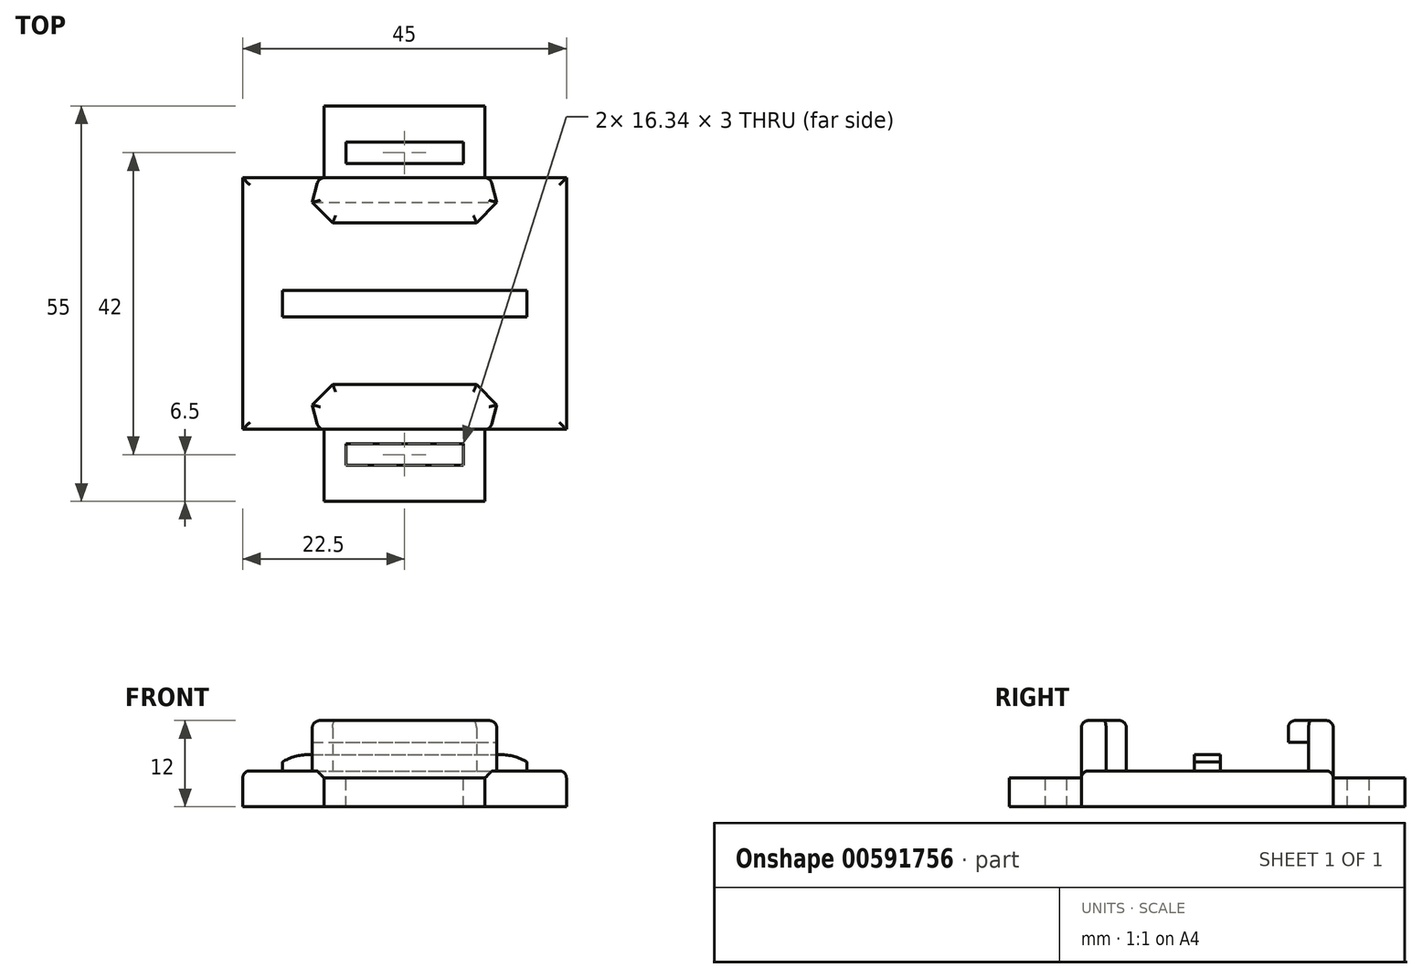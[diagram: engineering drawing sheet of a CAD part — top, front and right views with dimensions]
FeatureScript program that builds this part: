
annotation { "Feature Type Name" : "Feature", "Feature Type Description" : "" }
export const myFeature = defineFeature(function(context is Context, id is Id, definition is map)
    precondition{}
    {
        {
            var Q0;
            Q0=qCreatedBy(makeId("Top.planeOp"),FACE);
            var sketch = newSketch(context, id + "F0", { "sketchPlane" : qUnion([Q0])});
            skLineSegment(sketch, "E0.rect.bottom", {"start": v(-22.5, 17.5) * mm, "end": v(22.5, 17.5) * mm});
            skLineSegment(sketch, "E0.rect.top", {"start": v(-22.5, -17.5) * mm, "end": v(22.5, -17.5) * mm});
            skLineSegment(sketch, "E0.rect.left", {"start": v(-22.5, 17.5) * mm, "end": v(-22.5, -17.5) * mm});
            skLineSegment(sketch, "E0.rect.right", {"start": v(22.5, 17.5) * mm, "end": v(22.5, -17.5) * mm});
            skPoint(sketch, "E0.rect.middle", {"position": v(0, 0) * mm});
            skSolve(sketch);
        }
        {
            var Q0;
            Q0=makeQuery(id+"F0.imprint","IMPRINT",FACE,{"disambiguationData":[TD([[makeQuery(id+"F0.imprint","IMPRINT",EDGE,{"derivedFrom":sQuery(id+"F0.wireOp",EDGE,"E0.rect.bottom")}),-1.0]])]});
            extrude(context, id + "F1", {"entities" : qUnion([Q0]), "depth" : 5 * mm});
        }
        {
            var Q0;
            Q0=makeQuery(id+"F1.opExtrude","CAP_FACE",FACE,{"disambiguationData":[OSD([sQuery(id+"F0.wireOp",EDGE,"E0.rect.bottom"),sQuery(id+"F0.wireOp",EDGE,"E0.rect.top"),sQuery(id+"F0.wireOp",EDGE,"E0.rect.left"),sQuery(id+"F0.wireOp",EDGE,"E0.rect.right")])],"isStart":false});
            var sketch = newSketch(context, id + "F2", { "sketchPlane" : qUnion([Q0])});
            skLineSegment(sketch, "E1.rect.bottom", {"start": v(-17, 1.82) * mm, "end": v(17, 1.82) * mm});
            skLineSegment(sketch, "E1.rect.top", {"start": v(-17, -1.83) * mm, "end": v(17, -1.83) * mm});
            skLineSegment(sketch, "E1.rect.left", {"start": v(-17, 1.82) * mm, "end": v(-17, -1.83) * mm});
            skLineSegment(sketch, "E1.rect.right", {"start": v(17, 1.82) * mm, "end": v(17, -1.83) * mm});
            skPoint(sketch, "E1.rect.middle", {"position": v(0, 0) * mm});
            skSolve(sketch);
        }
        {
            var Q0;
            Q0=makeQuery(id+"F2.imprint","IMPRINT",FACE,{"disambiguationData":[TD([[makeQuery(id+"F2.imprint","IMPRINT",EDGE,{"derivedFrom":sQuery(id+"F2.wireOp",EDGE,"E1.rect.bottom")}),-1.0]])]});
            extrude(context, id + "F3", {"entities" : qUnion([Q0]), "operationType" : NewBodyOperationType.ADD, "depth" : 2.25 * mm});
        }
        {
            var Q0;
            Q0=makeQuery(id+"F3.opExtrude","SWEPT_FACE",FACE,{"disambiguationData":[OSD([sQuery(id+"F2.wireOp",EDGE,"E1.rect.top")])]});
            var sketch = newSketch(context, id + "F4", { "sketchPlane" : qUnion([Q0])});
            skLineSegment(sketch, "E2", {"start": v(-17, 7.25) * mm, "end": v(17, 7.25) * mm, "construction": true});
            skLineSegment(sketch, "E3.0", {"start": v(-17, 6.25) * mm, "end": v(17, 6.25) * mm});
            skArc(sketch, "E4", {"start": v(-13.26, 7.25) * mm, "mid": v(-15.2, 7) * mm, "end": v(-17, 6.25) * mm});
            skLineSegment(sketch, "E5", {"start": v(0, 0) * mm, "end": v(0, 15.47) * mm, "construction": true});
            skArc(sketch, "E6.0.MirrorCS", {"start": v(13.26, 7.25) * mm, "mid": v(15.2, 7) * mm, "end": v(17, 6.25) * mm});
            skLineSegment(sketch, "E7", {"start": v(-17, 6.25) * mm, "end": v(-18.16, 6.25) * mm});
            skLineSegment(sketch, "E8", {"start": v(-18.16, 6.25) * mm, "end": v(-18.16, 8.7) * mm});
            skLineSegment(sketch, "E9", {"start": v(-18.16, 8.7) * mm, "end": v(-13.25, 8.7) * mm});
            skLineSegment(sketch, "E10", {"start": v(-13.25, 8.7) * mm, "end": v(-13.26, 7.25) * mm});
            skLineSegment(sketch, "E11", {"start": v(13.26, 7.25) * mm, "end": v(13.26, 8.4) * mm});
            skLineSegment(sketch, "E12", {"start": v(13.26, 8.4) * mm, "end": v(18.11, 8.4) * mm});
            skLineSegment(sketch, "E13", {"start": v(18.11, 8.4) * mm, "end": v(18.11, 6.28) * mm});
            skLineSegment(sketch, "E14", {"start": v(18.11, 6.28) * mm, "end": v(17, 6.25) * mm});
            skSolve(sketch);
        }
        {
            var Q0;
            {var subQ0=sQuery(id+"F2.wireOp",EDGE,"E1.rect.top");var subQ1=makeQuery(id+"F3.opExtrude","CAP_EDGE",EDGE,{"disambiguationData":[OSD([subQ0])],"isStart":false});var subQ2=sQuery(id+"F4.wireOp",EDGE,"E4");var subQ3=makeQuery(id+"F4.imprint","INTERSECT",VERTEX,{"derivedFrom":[subQ1,subQ2]});var subQ6=makeQuery(id+"F4.imprint","IMPRINT",EDGE,{"disambiguationData":[TD([[subQ3,1.0]])],"derivedFrom":subQ1});var subQ8=sQuery(id+"F4.wireOp",EDGE,"E7");var subQ13=sQuery(id+"F4.wireOp",EDGE,"E6.0.MirrorCS");var subQ18=makeQuery(id+"F4.imprint","INTERSECT",VERTEX,{"derivedFrom":[subQ1,subQ13]});var subQ19=makeQuery(id+"F4.imprint","IMPRINT",EDGE,{"disambiguationData":[TD([[subQ18,-1.0]])],"derivedFrom":subQ1});var subQ20=sQuery(id+"F4.wireOp",EDGE,"E11");Q0=qUnion([makeQuery(id+"F4.imprint","IMPRINT",FACE,{"disambiguationData":[TD([[makeQuery(id+"F4.imprint","IMPRINT",EDGE,{"derivedFrom":subQ8}),-1.0]])]}),makeQuery(id+"F4.imprint","IMPRINT",FACE,{"disambiguationData":[TD([[subQ6,-1.0]])]}),makeQuery(id+"F4.imprint","IMPRINT",FACE,{"disambiguationData":[TD([[makeQuery(id+"F4.imprint","IMPRINT",EDGE,{"derivedFrom":subQ20}),-1.0]])]}),makeQuery(id+"F4.imprint","IMPRINT",FACE,{"disambiguationData":[TD([[subQ19,-1.0]])]})]);}
            extrude(context, id + "F5", {"entities" : qUnion([Q0]), "operationType" : NewBodyOperationType.REMOVE, "endBound" : BoundingType.THROUGH_ALL, "oppositeDirection" : true, "depth" : 25 * mm});
        }
        {
            var Q0;
            Q0=makeQuery(id+"F1.opExtrude","CAP_FACE",FACE,{"disambiguationData":[OSD([sQuery(id+"F0.wireOp",EDGE,"E0.rect.bottom"),sQuery(id+"F0.wireOp",EDGE,"E0.rect.top"),sQuery(id+"F0.wireOp",EDGE,"E0.rect.left"),sQuery(id+"F0.wireOp",EDGE,"E0.rect.right")])],"isStart":false});
            var sketch = newSketch(context, id + "F6", { "sketchPlane" : qUnion([Q0])});
            skLineSegment(sketch, "E15.rect.bottom", {"start": v(-11.94, 17.5) * mm, "end": v(11.94, 17.5) * mm, "construction": true});
            skPoint(sketch, "E15.rect.middle", {"position": v(0, 0) * mm});
            skLineSegment(sketch, "E16.0", {"start": v(-10, 11.25) * mm, "end": v(10, 11.25) * mm});
            skLineSegment(sketch, "E17", {"start": v(-10, 11.25) * mm, "end": v(-12.82, 14.08) * mm, "construction": true});
            skLineSegment(sketch, "E18.0.MirrorCS", {"start": v(10, 11.25) * mm, "end": v(12.82, 14.08) * mm, "construction": true});
            skLineSegment(sketch, "E19", {"start": v(10, 11.25) * mm, "end": v(12.82, 14.08) * mm});
            skLineSegment(sketch, "E20", {"start": v(11.94, 17.5) * mm, "end": v(-11.94, 17.5) * mm});
            skLineSegment(sketch, "E21", {"start": v(-12.82, 14.08) * mm, "end": v(-10, 11.25) * mm});
            skLineSegment(sketch, "E22.0.MirrorCS", {"start": v(-10, -11.25) * mm, "end": v(-12.82, -14.08) * mm, "construction": true});
            skLineSegment(sketch, "E22.1.MirrorCS", {"start": v(-11.94, -17.5) * mm, "end": v(11.94, -17.5) * mm, "construction": true});
            skLineSegment(sketch, "E22.2.MirrorCS", {"start": v(-11.94, -17.5) * mm, "end": v(11.94, -17.5) * mm, "construction": true});
            skLineSegment(sketch, "E22.4.MirrorCS", {"start": v(-10, -11.25) * mm, "end": v(-12.82, -14.08) * mm, "construction": true});
            skLineSegment(sketch, "E22.5.MirrorCS", {"start": v(10, -11.25) * mm, "end": v(12.82, -14.08) * mm, "construction": true});
            skLineSegment(sketch, "E22.7.MirrorCS", {"start": v(11.94, -17.5) * mm, "end": v(-11.94, -17.5) * mm});
            skLineSegment(sketch, "E22.9.MirrorCS", {"start": v(10, -11.25) * mm, "end": v(12.82, -14.08) * mm});
            skLineSegment(sketch, "E22.10.MirrorCS", {"start": v(-12.82, -14.08) * mm, "end": v(-10, -11.25) * mm});
            skLineSegment(sketch, "E22.12.MirrorCS", {"start": v(-10, -11.25) * mm, "end": v(10, -11.25) * mm});
            skLineSegment(sketch, "E23", {"start": v(12.82, 14.08) * mm, "end": v(11.94, 17.5) * mm});
            skLineSegment(sketch, "E24.0.MirrorCS", {"start": v(12.82, -14.08) * mm, "end": v(11.94, -17.5) * mm});
            skLineSegment(sketch, "E25.0.MirrorCS", {"start": v(-12.82, 14.08) * mm, "end": v(-11.94, 17.5) * mm});
            skLineSegment(sketch, "E26.0.MirrorCS", {"start": v(-12.82, -14.08) * mm, "end": v(-11.94, -17.5) * mm});
            skSolve(sketch);
        }
        {
            var Q0;
            {Q0=qUnion([makeQuery(id+"F6.imprint","IMPRINT",FACE,{"disambiguationData":[TD([[makeQuery(id+"F6.imprint","IMPRINT",EDGE,{"derivedFrom":sQuery(id+"F6.wireOp",EDGE,"E16.0")}),1.0]])]}),makeQuery(id+"F6.imprint","IMPRINT",FACE,{"disambiguationData":[TD([[makeQuery(id+"F6.imprint","IMPRINT",EDGE,{"derivedFrom":sQuery(id+"F6.wireOp",EDGE,"E22.7.MirrorCS")}),1.0]])]})]);}
            extrude(context, id + "F7", {"entities" : qUnion([Q0]), "operationType" : NewBodyOperationType.ADD, "depth" : 7 * mm});
        }
        {
            var Q0;
            Q0=qCreatedBy(makeId("Right.planeOp"),FACE);
            var sketch = newSketch(context, id + "F8", { "sketchPlane" : qUnion([Q0])});
            skLineSegment(sketch, "E27.0", {"start": v(14.1, 9) * mm, "end": v(14.1, 5) * mm});
            skLineSegment(sketch, "E28.bottom", {"start": v(14.1, 5) * mm, "end": v(10.15, 5) * mm});
            skLineSegment(sketch, "E28.top", {"start": v(14.1, 9) * mm, "end": v(10.15, 9) * mm});
            skLineSegment(sketch, "E28.left", {"start": v(14.1, 5) * mm, "end": v(14.1, 9) * mm});
            skLineSegment(sketch, "E28.right", {"start": v(10.15, 5) * mm, "end": v(10.15, 9) * mm});
            skLineSegment(sketch, "E29.0.MirrorCS", {"start": v(-14.1, 5) * mm, "end": v(-14.1, 9) * mm});
            skLineSegment(sketch, "E29.1.MirrorCS", {"start": v(-14.1, 9) * mm, "end": v(-14.1, 5) * mm});
            skLineSegment(sketch, "E29.2.MirrorCS", {"start": v(-14.1, 9) * mm, "end": v(-10.15, 9) * mm});
            skLineSegment(sketch, "E29.3.MirrorCS", {"start": v(-10.15, 5) * mm, "end": v(-10.15, 9) * mm});
            skLineSegment(sketch, "E29.4.MirrorCS", {"start": v(-14.1, 5) * mm, "end": v(-10.15, 5) * mm});
            skSolve(sketch);
        }
        {
            var Q0;
            {Q0=qUnion([makeQuery(id+"F8.imprint","IMPRINT",FACE,{"disambiguationData":[TD([[makeQuery(id+"F8.imprint","IMPRINT",EDGE,{"derivedFrom":sQuery(id+"F8.wireOp",EDGE,"E28.bottom")}),-1.0]])]}),makeQuery(id+"F8.imprint","IMPRINT",FACE,{"disambiguationData":[TD([[makeQuery(id+"F8.imprint","IMPRINT",EDGE,{"derivedFrom":sQuery(id+"F8.wireOp",EDGE,"E29.1.MirrorCS")}),1.0]])]})]);}
            extrude(context, id + "F9", {"entities" : qUnion([Q0]), "operationType" : NewBodyOperationType.REMOVE, "endBound" : BoundingType.SYMMETRIC, "oppositeDirection" : true, "depth" : 31.01 * mm});
        }
        {
            var Q0;
            Q0=makeQuery(id+"F7.opExtrude","CAP_FACE",FACE,{"disambiguationData":[OSD([sQuery(id+"F6.wireOp",EDGE,"E16.0"),sQuery(id+"F6.wireOp",EDGE,"E19"),sQuery(id+"F6.wireOp",EDGE,"E20"),sQuery(id+"F6.wireOp",EDGE,"E21"),sQuery(id+"F6.wireOp",EDGE,"E23"),sQuery(id+"F6.wireOp",EDGE,"E25.0.MirrorCS")])],"isStart":false});
            var Q1;
            Q1=makeQuery(id+"F7.opExtrude","CAP_FACE",FACE,{"disambiguationData":[OSD([sQuery(id+"F6.wireOp",EDGE,"E22.7.MirrorCS"),sQuery(id+"F6.wireOp",EDGE,"E22.9.MirrorCS"),sQuery(id+"F6.wireOp",EDGE,"E22.10.MirrorCS"),sQuery(id+"F6.wireOp",EDGE,"E22.12.MirrorCS"),sQuery(id+"F6.wireOp",EDGE,"E24.0.MirrorCS"),sQuery(id+"F6.wireOp",EDGE,"E26.0.MirrorCS")])],"isStart":false});
            var Q2;
            Q2=makeQuery(id+"F7.opExtrude","SWEPT_EDGE",EDGE,{"disambiguationData":[OSD([sQuery(id+"F0.wireOp",EDGE,"E0.rect.bottom"),sQuery(id+"F6.wireOp",EDGE,"E20"),sQuery(id+"F6.wireOp",EDGE,"E23")])]});
            var Q3;
            Q3=makeQuery(id+"F7.opExtrude","SWEPT_EDGE",EDGE,{"disambiguationData":[OSD([sQuery(id+"F0.wireOp",EDGE,"E0.rect.bottom"),sQuery(id+"F6.wireOp",EDGE,"E20"),sQuery(id+"F6.wireOp",EDGE,"E25.0.MirrorCS")])]});
            var Q4;
            Q4=makeQuery(id+"F7.opExtrude","SWEPT_EDGE",EDGE,{"disambiguationData":[OSD([sQuery(id+"F0.wireOp",EDGE,"E0.rect.top"),sQuery(id+"F6.wireOp",EDGE,"E22.7.MirrorCS"),sQuery(id+"F6.wireOp",EDGE,"E24.0.MirrorCS")])]});
            var Q5;
            Q5=makeQuery(id+"F7.opExtrude","SWEPT_EDGE",EDGE,{"disambiguationData":[OSD([sQuery(id+"F0.wireOp",EDGE,"E0.rect.top"),sQuery(id+"F6.wireOp",EDGE,"E22.7.MirrorCS"),sQuery(id+"F6.wireOp",EDGE,"E26.0.MirrorCS")])]});
            fillet(context, id + "F10", {"entities" : qUnion([Q0, Q1, Q2, Q3, Q4, Q5]), "radius" : 1 * mm, "tangentPropagation" : true, "allowEdgeOverflow" : false});
        }
        {
            var Q0;
            {var subQ0=sQuery(id+"F0.wireOp",EDGE,"E0.rect.top");var subQ1=sQuery(id+"F0.wireOp",EDGE,"E0.rect.right");Q0=makeQuery(id+"F7.boolean.opBoolean","SPLIT",EDGE,{"disambiguationData":[TD([makeQuery(id+"F1.opExtrude","SWEPT_FACE",FACE,{"disambiguationData":[OSD([subQ1])]})])],"derivedFrom":makeQuery(id+"F1.opExtrude","CAP_EDGE",EDGE,{"disambiguationData":[OSD([subQ0])],"isStart":false})});}
            var Q1;
            Q1=makeQuery(id+"F1.opExtrude","CAP_EDGE",EDGE,{"disambiguationData":[OSD([sQuery(id+"F0.wireOp",EDGE,"E0.rect.right")])],"isStart":false});
            var Q2;
            {var subQ0=sQuery(id+"F0.wireOp",EDGE,"E0.rect.bottom");var subQ1=sQuery(id+"F0.wireOp",EDGE,"E0.rect.right");Q2=makeQuery(id+"F7.boolean.opBoolean","SPLIT",EDGE,{"disambiguationData":[TD([makeQuery(id+"F1.opExtrude","SWEPT_FACE",FACE,{"disambiguationData":[OSD([subQ1])]})])],"derivedFrom":makeQuery(id+"F1.opExtrude","CAP_EDGE",EDGE,{"disambiguationData":[OSD([subQ0])],"isStart":false})});}
            var Q3;
            {var subQ0=sQuery(id+"F0.wireOp",EDGE,"E0.rect.bottom");var subQ1=sQuery(id+"F0.wireOp",EDGE,"E0.rect.left");Q3=makeQuery(id+"F7.boolean.opBoolean","SPLIT",EDGE,{"disambiguationData":[TD([makeQuery(id+"F1.opExtrude","SWEPT_FACE",FACE,{"disambiguationData":[OSD([subQ1])]})])],"derivedFrom":makeQuery(id+"F1.opExtrude","CAP_EDGE",EDGE,{"disambiguationData":[OSD([subQ0])],"isStart":false})});}
            var Q4;
            Q4=makeQuery(id+"F1.opExtrude","CAP_EDGE",EDGE,{"disambiguationData":[OSD([sQuery(id+"F0.wireOp",EDGE,"E0.rect.left")])],"isStart":false});
            var Q5;
            {var subQ0=sQuery(id+"F0.wireOp",EDGE,"E0.rect.top");var subQ1=sQuery(id+"F0.wireOp",EDGE,"E0.rect.left");Q5=makeQuery(id+"F7.boolean.opBoolean","SPLIT",EDGE,{"disambiguationData":[TD([makeQuery(id+"F1.opExtrude","SWEPT_FACE",FACE,{"disambiguationData":[OSD([subQ1])]})])],"derivedFrom":makeQuery(id+"F1.opExtrude","CAP_EDGE",EDGE,{"disambiguationData":[OSD([subQ0])],"isStart":false})});}
            fillet(context, id + "F11", {"entities" : qUnion([Q0, Q1, Q2, Q3, Q4, Q5]), "radius" : 1 * mm, "allowEdgeOverflow" : false});
        }
        {
            var Q0;
            Q0=makeQuery(id+"F7.boolean.opBoolean","MERGE",FACE,{"derivedFrom":[makeQuery(id+"F1.opExtrude","SWEPT_FACE",FACE,{"disambiguationData":[OSD([sQuery(id+"F0.wireOp",EDGE,"E0.rect.bottom")])]}),makeQuery(id+"F7.opExtrude","SWEPT_FACE",FACE,{"disambiguationData":[OSD([sQuery(id+"F6.wireOp",EDGE,"E20")])]})]});
            var sketch = newSketch(context, id + "F12", { "sketchPlane" : qUnion([Q0])});
            skLineSegment(sketch, "E30.0", {"start": v(22.5, 0) * mm, "end": v(-22.5, 0) * mm});
            skLineSegment(sketch, "E31.0", {"start": v(11.17, 11) * mm, "end": v(-11.17, 11) * mm});
            skLineSegment(sketch, "E32", {"start": v(-11.17, 11) * mm, "end": v(-11.17, 0) * mm, "construction": true});
            skLineSegment(sketch, "E33", {"start": v(11.17, 11) * mm, "end": v(11.17, 0) * mm, "construction": true});
            skLineSegment(sketch, "E34", {"start": v(-11.17, 4) * mm, "end": v(11.17, 4) * mm});
            skLineSegment(sketch, "E35", {"start": v(11.17, 4) * mm, "end": v(11.17, 0) * mm});
            skLineSegment(sketch, "E36", {"start": v(-11.17, 0) * mm, "end": v(-11.17, 4) * mm});
            skSolve(sketch);
        }
        {
            var Q0;
            Q0 = qSketchRegion(id + "F12", true);
            extrude(context, id + "F13", {"entities" : qUnion([Q0]), "operationType" : NewBodyOperationType.ADD, "depth" : 10 * mm, "offsetDistance" : 25 * mm});
        }
        {
            var Q0;
            Q0=makeQuery(id+"F7.boolean.opBoolean","MERGE",FACE,{"derivedFrom":[makeQuery(id+"F1.opExtrude","SWEPT_FACE",FACE,{"disambiguationData":[OSD([sQuery(id+"F0.wireOp",EDGE,"E0.rect.top")])]}),makeQuery(id+"F7.opExtrude","SWEPT_FACE",FACE,{"disambiguationData":[OSD([sQuery(id+"F6.wireOp",EDGE,"E22.7.MirrorCS")])]})]});
            var sketch = newSketch(context, id + "F14", { "sketchPlane" : qUnion([Q0])});
            skLineSegment(sketch, "E37.0", {"start": v(11.17, 11) * mm, "end": v(-11.17, 11) * mm});
            skLineSegment(sketch, "E38.0", {"start": v(-22.5, 0) * mm, "end": v(22.5, 0) * mm});
            skLineSegment(sketch, "E39", {"start": v(-11.17, 11) * mm, "end": v(-11.17, 0) * mm, "construction": true});
            skLineSegment(sketch, "E40", {"start": v(11.17, 11) * mm, "end": v(11.17, 0) * mm, "construction": true});
            skPoint(sketch, "E40.endSnap0", {"position": v(11.17, 7.5) * mm});
            skLineSegment(sketch, "E41", {"start": v(-11.17, 4) * mm, "end": v(11.17, 4) * mm});
            skLineSegment(sketch, "E42", {"start": v(11.17, 4) * mm, "end": v(11.17, 0) * mm});
            skLineSegment(sketch, "E43", {"start": v(-11.17, 0) * mm, "end": v(-11.17, 4) * mm});
            skSolve(sketch);
        }
        {
            var Q0;
            Q0=makeQuery(id+"F14.imprint","IMPRINT",FACE,{"disambiguationData":[TD([[makeQuery(id+"F14.imprint","IMPRINT",EDGE,{"derivedFrom":sQuery(id+"F14.wireOp",EDGE,"E41")}),-1.0]])]});
            extrude(context, id + "F15", {"entities" : qUnion([Q0]), "operationType" : NewBodyOperationType.ADD, "depth" : 10 * mm, "offsetDistance" : 25 * mm});
        }
        {
            var Q0;
            Q0=makeQuery(id+"F15.opExtrude","SWEPT_FACE",FACE,{"disambiguationData":[OSD([sQuery(id+"F14.wireOp",EDGE,"E41")])]});
            var sketch = newSketch(context, id + "F16", { "sketchPlane" : qUnion([Q0])});
            skLineSegment(sketch, "E44.0", {"start": v(-11.17, -27.5) * mm, "end": v(11.17, -27.5) * mm});
            skLineSegment(sketch, "E45.0", {"start": v(-11.17, -17.5) * mm, "end": v(11.17, -17.5) * mm});
            skLineSegment(sketch, "E46.0", {"start": v(-11.17, -27.5) * mm, "end": v(-11.17, -17.5) * mm});
            skLineSegment(sketch, "E47.0", {"start": v(11.17, -27.5) * mm, "end": v(11.17, -17.5) * mm});
            skLineSegment(sketch, "E48.bottom", {"start": v(-11.17, -22.5) * mm, "end": v(11.17, -22.5) * mm});
            skLineSegment(sketch, "E48.top", {"start": v(-11.17, -19.5) * mm, "end": v(11.17, -19.5) * mm});
            skLineSegment(sketch, "E48.left", {"start": v(-11.17, -22.5) * mm, "end": v(-11.17, -19.5) * mm});
            skLineSegment(sketch, "E48.right", {"start": v(11.17, -22.5) * mm, "end": v(11.17, -19.5) * mm});
            skLineSegment(sketch, "E49", {"start": v(-8.17, -19.5) * mm, "end": v(-8.17, -22.5) * mm});
            skLineSegment(sketch, "E50", {"start": v(8.17, -19.5) * mm, "end": v(8.17, -22.5) * mm});
            skLineSegment(sketch, "E51", {"start": v(-11.17, -21) * mm, "end": v(-8.17, -21) * mm, "construction": true});
            skLineSegment(sketch, "E52", {"start": v(8.17, -21) * mm, "end": v(11.17, -21) * mm, "construction": true});
            skSolve(sketch);
        }
        {
            var Q0;
            {var subQ0=sQuery(id+"F16.wireOp",EDGE,"E49");Q0=makeQuery(id+"F16.imprint","IMPRINT",FACE,{"disambiguationData":[TD([[makeQuery(id+"F16.imprint","IMPRINT",EDGE,{"derivedFrom":subQ0}),1.0]])]});}
            extrude(context, id + "F17", {"entities" : qUnion([Q0]), "operationType" : NewBodyOperationType.REMOVE, "oppositeDirection" : true, "depth" : 25 * mm, "offsetDistance" : 25 * mm});
        }
        {
            var Q0;
            Q0=makeQuery(id+"F13.opExtrude","SWEPT_FACE",FACE,{"disambiguationData":[OSD([sQuery(id+"F12.wireOp",EDGE,"E34")])]});
            var sketch = newSketch(context, id + "F18", { "sketchPlane" : qUnion([Q0])});
            skLineSegment(sketch, "E53", {"start": v(-11.17, 22.5) * mm, "end": v(11.17, 22.5) * mm});
            skLineSegment(sketch, "E54", {"start": v(-11.17, 19.5) * mm, "end": v(11.17, 19.5) * mm});
            skLineSegment(sketch, "E55", {"start": v(-8.55, 22.5) * mm, "end": v(-8.55, 19.5) * mm, "construction": true});
            skLineSegment(sketch, "E56", {"start": v(-8.17, 19.5) * mm, "end": v(-8.17, 22.5) * mm});
            skLineSegment(sketch, "E57", {"start": v(8.17, 19.5) * mm, "end": v(8.17, 22.5) * mm});
            skLineSegment(sketch, "E58", {"start": v(-11.17, 20.93) * mm, "end": v(-8.17, 20.93) * mm, "construction": true});
            skLineSegment(sketch, "E59", {"start": v(11.17, 20.72) * mm, "end": v(8.17, 20.72) * mm, "construction": true});
            skSolve(sketch);
        }
        {
            var Q0;
            {var subQ0=sQuery(id+"F18.wireOp",EDGE,"E56");Q0=makeQuery(id+"F18.imprint","IMPRINT",FACE,{"disambiguationData":[TD([[makeQuery(id+"F18.imprint","IMPRINT",EDGE,{"derivedFrom":subQ0}),-1.0]])]});}
            extrude(context, id + "F19", {"entities" : qUnion([Q0]), "operationType" : NewBodyOperationType.REMOVE, "oppositeDirection" : true, "depth" : 25 * mm, "offsetDistance" : 25 * mm});
        }
    });
